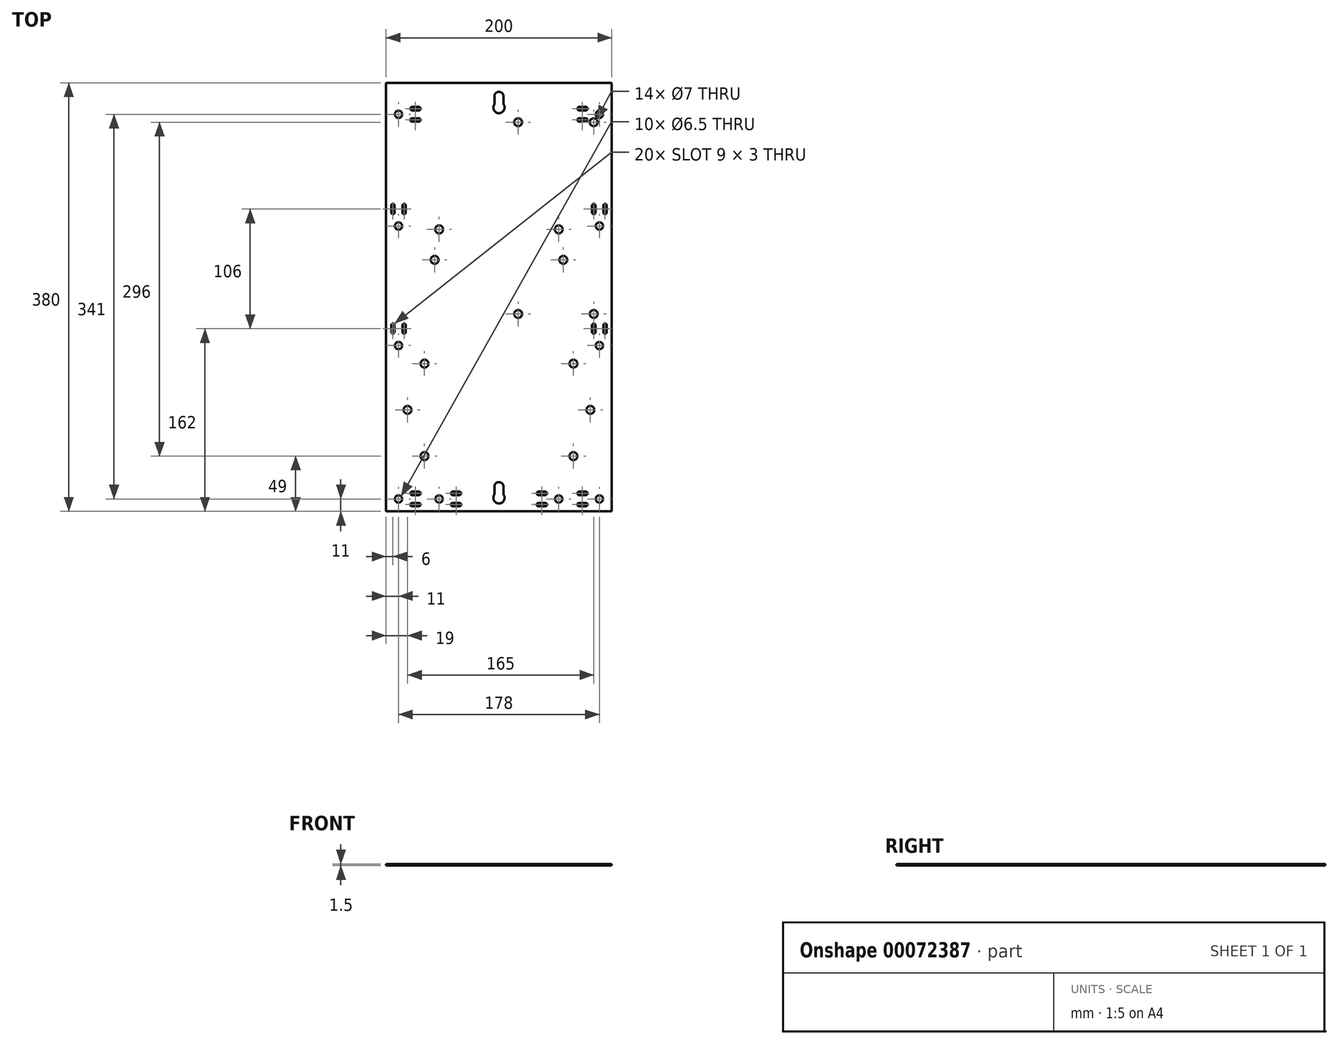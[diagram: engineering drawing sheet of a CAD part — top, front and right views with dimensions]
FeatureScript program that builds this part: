
annotation { "Feature Type Name" : "Feature", "Feature Type Description" : "" }
export const myFeature = defineFeature(function(context is Context, id is Id, definition is map)
    precondition{}
    {
        {
            var Q0;
            Q0=qCreatedBy(makeId("Top.planeOp"),FACE);
            var sketch = newSketch(context, id + "F0", { "sketchPlane" : qUnion([Q0])});
            skLineSegment(sketch, "E0.rect.bottom", {"start": v(100, 190) * mm, "end": v(-100, 190) * mm});
            skLineSegment(sketch, "E0.rect.top", {"start": v(100, -190) * mm, "end": v(-100, -190) * mm});
            skLineSegment(sketch, "E0.rect.left", {"start": v(100, 190) * mm, "end": v(100, -190) * mm});
            skLineSegment(sketch, "E0.rect.right", {"start": v(-100, 190) * mm, "end": v(-100, -190) * mm});
            skPoint(sketch, "E0.rect.middle", {"position": v(0, 0) * mm});
            skLineSegment(sketch, "E1", {"start": v(0, -190) * mm, "end": v(0, 190) * mm, "construction": true});
            skCircle(sketch, "E2", {"center": v(-89, 162) * mm, "radius": 3.25 * mm});
            skCircle(sketch, "E3", {"center": v(-89, 63) * mm, "radius": 3.25 * mm});
            skCircle(sketch, "E4", {"center": v(-89, -43) * mm, "radius": 3.25 * mm});
            skCircle(sketch, "E5", {"center": v(-89, -179) * mm, "radius": 3.25 * mm});
            skCircle(sketch, "E6", {"center": v(-66, -141) * mm, "radius": 3.5 * mm});
            skCircle(sketch, "E7", {"center": v(-81, -100) * mm, "radius": 3.5 * mm});
            skCircle(sketch, "E8", {"center": v(-66, -59) * mm, "radius": 3.5 * mm});
            skCircle(sketch, "E9", {"center": v(-57, 33) * mm, "radius": 3.5 * mm});
            skCircle(sketch, "E10", {"center": v(-53, 60) * mm, "radius": 3.5 * mm});
            skCircle(sketch, "E11", {"center": v(-53, -179) * mm, "radius": 3.25 * mm});
            skArc(sketch, "E12", {"start": v(-77, -172.5) * mm, "mid": v(-78.5, -174) * mm, "end": v(-77, -175.5) * mm});
            skArc(sketch, "E13", {"start": v(-71, -175.5) * mm, "mid": v(-69.5, -174) * mm, "end": v(-71, -172.5) * mm});
            skLineSegment(sketch, "E14", {"start": v(-77, -172.5) * mm, "end": v(-71, -172.5) * mm});
            skLineSegment(sketch, "E15", {"start": v(-71, -175.5) * mm, "end": v(-77, -175.5) * mm});
            skLineSegment(sketch, "E16", {"start": v(-89, -179) * mm, "end": v(-66.78, -179) * mm, "construction": true});
            skArc(sketch, "E17.MirrorCS", {"start": v(-71, -182.5) * mm, "mid": v(-69.5, -184) * mm, "end": v(-71, -185.5) * mm});
            skLineSegment(sketch, "E18.MirrorCS", {"start": v(-77, -185.5) * mm, "end": v(-71, -185.5) * mm});
            skLineSegment(sketch, "E19.MirrorCS", {"start": v(-71, -182.5) * mm, "end": v(-77, -182.5) * mm});
            skArc(sketch, "E20.MirrorCS", {"start": v(-77, -185.5) * mm, "mid": v(-78.5, -184) * mm, "end": v(-77, -182.5) * mm});
            skArc(sketch, "E21.1.0.0", {"start": v(-41, -172.5) * mm, "mid": v(-42.5, -174) * mm, "end": v(-41, -175.5) * mm});
            skLineSegment(sketch, "E21.1.0.1", {"start": v(-41, -172.5) * mm, "end": v(-35, -172.5) * mm});
            skLineSegment(sketch, "E21.1.0.2", {"start": v(-35, -182.5) * mm, "end": v(-41, -182.5) * mm});
            skArc(sketch, "E21.1.0.3", {"start": v(-41, -185.5) * mm, "mid": v(-42.5, -184) * mm, "end": v(-41, -182.5) * mm});
            skLineSegment(sketch, "E21.1.0.4", {"start": v(-41, -185.5) * mm, "end": v(-35, -185.5) * mm});
            skArc(sketch, "E21.1.0.5", {"start": v(-35, -182.5) * mm, "mid": v(-33.5, -184) * mm, "end": v(-35, -185.5) * mm});
            skLineSegment(sketch, "E21.1.0.6", {"start": v(-35, -175.5) * mm, "end": v(-41, -175.5) * mm});
            skArc(sketch, "E21.1.0.7", {"start": v(-35, -175.5) * mm, "mid": v(-33.5, -174) * mm, "end": v(-35, -172.5) * mm});
            skLineSegment(sketch, "E21.direction1", {"start": v(-77, -175.5) * mm, "end": v(-41, -175.5) * mm, "construction": true});
            skArc(sketch, "E22", {"start": v(-95.5, -31) * mm, "mid": v(-94, -32.5) * mm, "end": v(-92.5, -31) * mm});
            skArc(sketch, "E23", {"start": v(-92.5, -25) * mm, "mid": v(-94, -23.5) * mm, "end": v(-95.5, -25) * mm});
            skLineSegment(sketch, "E24", {"start": v(-95.5, -31) * mm, "end": v(-95.5, -25) * mm});
            skLineSegment(sketch, "E25", {"start": v(-92.5, -25) * mm, "end": v(-92.5, -31) * mm});
            skLineSegment(sketch, "E26", {"start": v(-89, -43) * mm, "end": v(-89, -23.5) * mm, "construction": true});
            skArc(sketch, "E27.MirrorCS", {"start": v(-85.5, -25) * mm, "mid": v(-84, -23.5) * mm, "end": v(-82.5, -25) * mm});
            skLineSegment(sketch, "E28.MirrorCS", {"start": v(-85.5, -25) * mm, "end": v(-85.5, -31) * mm});
            skLineSegment(sketch, "E29.MirrorCS", {"start": v(-82.5, -31) * mm, "end": v(-82.5, -25) * mm});
            skArc(sketch, "E30.MirrorCS", {"start": v(-82.5, -31) * mm, "mid": v(-84, -32.5) * mm, "end": v(-85.5, -31) * mm});
            skLineSegment(sketch, "E31.0.1.0", {"start": v(-85.5, 81) * mm, "end": v(-85.5, 75) * mm});
            skLineSegment(sketch, "E31.0.1.1", {"start": v(-92.5, 81) * mm, "end": v(-92.5, 75) * mm});
            skLineSegment(sketch, "E31.0.1.2", {"start": v(-95.5, 75) * mm, "end": v(-95.5, 81) * mm});
            skArc(sketch, "E31.0.1.3", {"start": v(-95.5, 75) * mm, "mid": v(-94, 73.5) * mm, "end": v(-92.5, 75) * mm});
            skLineSegment(sketch, "E31.0.1.4", {"start": v(-82.5, 75) * mm, "end": v(-82.5, 81) * mm});
            skArc(sketch, "E31.0.1.5", {"start": v(-82.5, 75) * mm, "mid": v(-84, 73.5) * mm, "end": v(-85.5, 75) * mm});
            skArc(sketch, "E31.0.1.6", {"start": v(-85.5, 81) * mm, "mid": v(-84, 82.5) * mm, "end": v(-82.5, 81) * mm});
            skArc(sketch, "E31.0.1.7", {"start": v(-92.5, 81) * mm, "mid": v(-94, 82.5) * mm, "end": v(-95.5, 81) * mm});
            skLineSegment(sketch, "E31.direction1", {"start": v(-85.5, -31) * mm, "end": v(-60.5, -31) * mm, "construction": true});
            skLineSegment(sketch, "E31.direction2", {"start": v(-85.5, -31) * mm, "end": v(-85.5, 75) * mm, "construction": true});
            skArc(sketch, "E32", {"start": v(-77, 168.5) * mm, "mid": v(-78.5, 167) * mm, "end": v(-77, 165.5) * mm});
            skArc(sketch, "E33", {"start": v(-71, 165.5) * mm, "mid": v(-69.5, 167) * mm, "end": v(-71, 168.5) * mm});
            skLineSegment(sketch, "E34", {"start": v(-77, 168.5) * mm, "end": v(-71, 168.5) * mm});
            skLineSegment(sketch, "E35", {"start": v(-71, 165.5) * mm, "end": v(-77, 165.5) * mm});
            skLineSegment(sketch, "E36", {"start": v(-89, 162) * mm, "end": v(-66.49, 162) * mm, "construction": true});
            skLineSegment(sketch, "E37.MirrorCS", {"start": v(-71, 158.5) * mm, "end": v(-77, 158.5) * mm});
            skLineSegment(sketch, "E38.MirrorCS", {"start": v(-77, 155.5) * mm, "end": v(-71, 155.5) * mm});
            skArc(sketch, "E39.MirrorCS", {"start": v(-71, 158.5) * mm, "mid": v(-69.5, 157) * mm, "end": v(-71, 155.5) * mm});
            skArc(sketch, "E40.MirrorCS", {"start": v(-77, 155.5) * mm, "mid": v(-78.5, 157) * mm, "end": v(-77, 158.5) * mm});
            skArc(sketch, "E41.MirrorCS", {"start": v(92.5, -25) * mm, "mid": v(94, -23.5) * mm, "end": v(95.5, -25) * mm});
            skArc(sketch, "E42.MirrorCS", {"start": v(95.5, -31) * mm, "mid": v(94, -32.5) * mm, "end": v(92.5, -31) * mm});
            skLineSegment(sketch, "E43.MirrorCS", {"start": v(95.5, -31) * mm, "end": v(95.5, -25) * mm});
            skLineSegment(sketch, "E44.MirrorCS", {"start": v(92.5, -25) * mm, "end": v(92.5, -31) * mm});
            skLineSegment(sketch, "E45.MirrorCS", {"start": v(71, -175.5) * mm, "end": v(77, -175.5) * mm});
            skLineSegment(sketch, "E46.MirrorCS", {"start": v(41, -172.5) * mm, "end": v(35, -172.5) * mm});
            skArc(sketch, "E47.MirrorCS", {"start": v(82.5, -31) * mm, "mid": v(84, -32.5) * mm, "end": v(85.5, -31) * mm});
            skArc(sketch, "E48.MirrorCS", {"start": v(92.5, 81) * mm, "mid": v(94, 82.5) * mm, "end": v(95.5, 81) * mm});
            skLineSegment(sketch, "E49.MirrorCS", {"start": v(77, -172.5) * mm, "end": v(71, -172.5) * mm});
            skArc(sketch, "E50.MirrorCS", {"start": v(41, -172.5) * mm, "mid": v(42.5, -174) * mm, "end": v(41, -175.5) * mm});
            skLineSegment(sketch, "E51.MirrorCS", {"start": v(82.5, -31) * mm, "end": v(82.5, -25) * mm});
            skArc(sketch, "E52.MirrorCS", {"start": v(77, -172.5) * mm, "mid": v(78.5, -174) * mm, "end": v(77, -175.5) * mm});
            skArc(sketch, "E53.MirrorCS", {"start": v(85.5, -25) * mm, "mid": v(84, -23.5) * mm, "end": v(82.5, -25) * mm});
            skLineSegment(sketch, "E54.MirrorCS", {"start": v(77, 168.5) * mm, "end": v(71, 168.5) * mm});
            skLineSegment(sketch, "E55.MirrorCS", {"start": v(71, -182.5) * mm, "end": v(77, -182.5) * mm});
            skLineSegment(sketch, "E56.MirrorCS", {"start": v(35, -182.5) * mm, "end": v(41, -182.5) * mm});
            skLineSegment(sketch, "E57.MirrorCS", {"start": v(85.5, 81) * mm, "end": v(85.5, 75) * mm});
            skLineSegment(sketch, "E58.MirrorCS", {"start": v(95.5, 75) * mm, "end": v(95.5, 81) * mm});
            skLineSegment(sketch, "E59.MirrorCS", {"start": v(77, -185.5) * mm, "end": v(71, -185.5) * mm});
            skArc(sketch, "E60.MirrorCS", {"start": v(95.5, 75) * mm, "mid": v(94, 73.5) * mm, "end": v(92.5, 75) * mm});
            skLineSegment(sketch, "E61.MirrorCS", {"start": v(85.5, -25) * mm, "end": v(85.5, -31) * mm});
            skArc(sketch, "E62.MirrorCS", {"start": v(77, 168.5) * mm, "mid": v(78.5, 167) * mm, "end": v(77, 165.5) * mm});
            skLineSegment(sketch, "E63.MirrorCS", {"start": v(92.5, 81) * mm, "end": v(92.5, 75) * mm});
            skArc(sketch, "E64.MirrorCS", {"start": v(71, -182.5) * mm, "mid": v(69.5, -184) * mm, "end": v(71, -185.5) * mm});
            skArc(sketch, "E65.MirrorCS", {"start": v(71, 165.5) * mm, "mid": v(69.5, 167) * mm, "end": v(71, 168.5) * mm});
            skLineSegment(sketch, "E66.MirrorCS", {"start": v(71, 165.5) * mm, "end": v(77, 165.5) * mm});
            skLineSegment(sketch, "E67.MirrorCS", {"start": v(35, -175.5) * mm, "end": v(41, -175.5) * mm});
            skLineSegment(sketch, "E68.MirrorCS", {"start": v(71, 158.5) * mm, "end": v(77, 158.5) * mm});
            skArc(sketch, "E69.MirrorCS", {"start": v(35, -175.5) * mm, "mid": v(33.5, -174) * mm, "end": v(35, -172.5) * mm});
            skArc(sketch, "E70.MirrorCS", {"start": v(82.5, 75) * mm, "mid": v(84, 73.5) * mm, "end": v(85.5, 75) * mm});
            skArc(sketch, "E71.MirrorCS", {"start": v(85.5, 81) * mm, "mid": v(84, 82.5) * mm, "end": v(82.5, 81) * mm});
            skLineSegment(sketch, "E72.MirrorCS", {"start": v(77, 155.5) * mm, "end": v(71, 155.5) * mm});
            skArc(sketch, "E73.MirrorCS", {"start": v(77, 155.5) * mm, "mid": v(78.5, 157) * mm, "end": v(77, 158.5) * mm});
            skLineSegment(sketch, "E74.MirrorCS", {"start": v(41, -185.5) * mm, "end": v(35, -185.5) * mm});
            skArc(sketch, "E75.MirrorCS", {"start": v(71, -175.5) * mm, "mid": v(69.5, -174) * mm, "end": v(71, -172.5) * mm});
            skArc(sketch, "E76.MirrorCS", {"start": v(35, -182.5) * mm, "mid": v(33.5, -184) * mm, "end": v(35, -185.5) * mm});
            skArc(sketch, "E77.MirrorCS", {"start": v(41, -185.5) * mm, "mid": v(42.5, -184) * mm, "end": v(41, -182.5) * mm});
            skArc(sketch, "E78.MirrorCS", {"start": v(77, -185.5) * mm, "mid": v(78.5, -184) * mm, "end": v(77, -182.5) * mm});
            skLineSegment(sketch, "E79.MirrorCS", {"start": v(82.5, 75) * mm, "end": v(82.5, 81) * mm});
            skArc(sketch, "E80.MirrorCS", {"start": v(71, 158.5) * mm, "mid": v(69.5, 157) * mm, "end": v(71, 155.5) * mm});
            skLineSegment(sketch, "E81.MirrorCS", {"start": v(89, -43) * mm, "end": v(89, -23.5) * mm, "construction": true});
            skLineSegment(sketch, "E82.MirrorCS", {"start": v(89, 162) * mm, "end": v(66.49, 162) * mm, "construction": true});
            skCircle(sketch, "E83.MirrorC", {"center": v(53, -179) * mm, "radius": 3.25 * mm});
            skLineSegment(sketch, "E84.MirrorCS", {"start": v(77, -175.5) * mm, "end": v(41, -175.5) * mm, "construction": true});
            skLineSegment(sketch, "E85.MirrorCS", {"start": v(89, -179) * mm, "end": v(66.78, -179) * mm, "construction": true});
            skCircle(sketch, "E86.MirrorC", {"center": v(89, -43) * mm, "radius": 3.25 * mm});
            skCircle(sketch, "E87.MirrorC", {"center": v(89, -179) * mm, "radius": 3.25 * mm});
            skCircle(sketch, "E88.MirrorC", {"center": v(89, 162) * mm, "radius": 3.25 * mm});
            skLineSegment(sketch, "E89.MirrorCS", {"start": v(85.5, -31) * mm, "end": v(85.5, 75) * mm, "construction": true});
            skLineSegment(sketch, "E90.MirrorCS", {"start": v(85.5, -31) * mm, "end": v(60.5, -31) * mm, "construction": true});
            skCircle(sketch, "E91.MirrorC", {"center": v(53, 60) * mm, "radius": 3.5 * mm});
            skCircle(sketch, "E92.MirrorC", {"center": v(89, 63) * mm, "radius": 3.25 * mm});
            skCircle(sketch, "E93.MirrorC", {"center": v(66, -141) * mm, "radius": 3.5 * mm});
            skCircle(sketch, "E94.MirrorC", {"center": v(81, -100) * mm, "radius": 3.5 * mm});
            skCircle(sketch, "E95.MirrorC", {"center": v(57, 33) * mm, "radius": 3.5 * mm});
            skCircle(sketch, "E96.MirrorC", {"center": v(66, -59) * mm, "radius": 3.5 * mm});
            skSolve(sketch);
        }
        {
            var Q0;
            Q0=makeQuery(id+"F0.imprint","IMPRINT",FACE,{"disambiguationData":[TD([[makeQuery(id+"F0.imprint","IMPRINT",EDGE,{"derivedFrom":sQuery(id+"F0.wireOp",EDGE,"E0.rect.bottom")}),1.0]])]});
            extrude(context, id + "F1", {"entities" : qUnion([Q0]), "depth" : 1.5 * mm});
        }
        {
            var Q0;
            Q0=makeQuery(id+"F1.opExtrude","CAP_FACE",FACE,{"disambiguationData":[OSD([sQuery(id+"F0.wireOp",EDGE,"E0.rect.bottom"),sQuery(id+"F0.wireOp",EDGE,"E0.rect.top"),sQuery(id+"F0.wireOp",EDGE,"E0.rect.left"),sQuery(id+"F0.wireOp",EDGE,"E0.rect.right"),sQuery(id+"F0.wireOp",EDGE,"E2"),sQuery(id+"F0.wireOp",EDGE,"E3"),sQuery(id+"F0.wireOp",EDGE,"E4"),sQuery(id+"F0.wireOp",EDGE,"E5"),sQuery(id+"F0.wireOp",EDGE,"E6"),sQuery(id+"F0.wireOp",EDGE,"E7"),sQuery(id+"F0.wireOp",EDGE,"E8"),sQuery(id+"F0.wireOp",EDGE,"E9"),sQuery(id+"F0.wireOp",EDGE,"E10"),sQuery(id+"F0.wireOp",EDGE,"E11"),sQuery(id+"F0.wireOp",EDGE,"E12"),sQuery(id+"F0.wireOp",EDGE,"E13"),sQuery(id+"F0.wireOp",EDGE,"E14"),sQuery(id+"F0.wireOp",EDGE,"E15"),sQuery(id+"F0.wireOp",EDGE,"E17.MirrorCS"),sQuery(id+"F0.wireOp",EDGE,"E18.MirrorCS"),sQuery(id+"F0.wireOp",EDGE,"E19.MirrorCS"),sQuery(id+"F0.wireOp",EDGE,"E20.MirrorCS"),sQuery(id+"F0.wireOp",EDGE,"E21.1.0.0"),sQuery(id+"F0.wireOp",EDGE,"E21.1.0.1"),sQuery(id+"F0.wireOp",EDGE,"E21.1.0.2"),sQuery(id+"F0.wireOp",EDGE,"E21.1.0.3"),sQuery(id+"F0.wireOp",EDGE,"E21.1.0.4"),sQuery(id+"F0.wireOp",EDGE,"E21.1.0.5"),sQuery(id+"F0.wireOp",EDGE,"E21.1.0.6"),sQuery(id+"F0.wireOp",EDGE,"E21.1.0.7"),sQuery(id+"F0.wireOp",EDGE,"E22"),sQuery(id+"F0.wireOp",EDGE,"E23"),sQuery(id+"F0.wireOp",EDGE,"E24"),sQuery(id+"F0.wireOp",EDGE,"E25"),sQuery(id+"F0.wireOp",EDGE,"E27.MirrorCS"),sQuery(id+"F0.wireOp",EDGE,"E28.MirrorCS"),sQuery(id+"F0.wireOp",EDGE,"E29.MirrorCS"),sQuery(id+"F0.wireOp",EDGE,"E30.MirrorCS"),sQuery(id+"F0.wireOp",EDGE,"E31.0.1.0"),sQuery(id+"F0.wireOp",EDGE,"E31.0.1.1"),sQuery(id+"F0.wireOp",EDGE,"E31.0.1.2"),sQuery(id+"F0.wireOp",EDGE,"E31.0.1.3"),sQuery(id+"F0.wireOp",EDGE,"E31.0.1.4"),sQuery(id+"F0.wireOp",EDGE,"E31.0.1.5"),sQuery(id+"F0.wireOp",EDGE,"E31.0.1.6"),sQuery(id+"F0.wireOp",EDGE,"E31.0.1.7"),sQuery(id+"F0.wireOp",EDGE,"E32"),sQuery(id+"F0.wireOp",EDGE,"E33"),sQuery(id+"F0.wireOp",EDGE,"E34"),sQuery(id+"F0.wireOp",EDGE,"E35"),sQuery(id+"F0.wireOp",EDGE,"E37.MirrorCS"),sQuery(id+"F0.wireOp",EDGE,"E38.MirrorCS"),sQuery(id+"F0.wireOp",EDGE,"E39.MirrorCS"),sQuery(id+"F0.wireOp",EDGE,"E40.MirrorCS"),sQuery(id+"F0.wireOp",EDGE,"E41.MirrorCS"),sQuery(id+"F0.wireOp",EDGE,"E42.MirrorCS"),sQuery(id+"F0.wireOp",EDGE,"E43.MirrorCS"),sQuery(id+"F0.wireOp",EDGE,"E44.MirrorCS"),sQuery(id+"F0.wireOp",EDGE,"E45.MirrorCS"),sQuery(id+"F0.wireOp",EDGE,"E46.MirrorCS"),sQuery(id+"F0.wireOp",EDGE,"E47.MirrorCS"),sQuery(id+"F0.wireOp",EDGE,"E48.MirrorCS"),sQuery(id+"F0.wireOp",EDGE,"E49.MirrorCS"),sQuery(id+"F0.wireOp",EDGE,"E50.MirrorCS"),sQuery(id+"F0.wireOp",EDGE,"E51.MirrorCS"),sQuery(id+"F0.wireOp",EDGE,"E52.MirrorCS"),sQuery(id+"F0.wireOp",EDGE,"E53.MirrorCS"),sQuery(id+"F0.wireOp",EDGE,"E54.MirrorCS"),sQuery(id+"F0.wireOp",EDGE,"E55.MirrorCS"),sQuery(id+"F0.wireOp",EDGE,"E56.MirrorCS"),sQuery(id+"F0.wireOp",EDGE,"E57.MirrorCS"),sQuery(id+"F0.wireOp",EDGE,"E58.MirrorCS"),sQuery(id+"F0.wireOp",EDGE,"E59.MirrorCS"),sQuery(id+"F0.wireOp",EDGE,"E60.MirrorCS"),sQuery(id+"F0.wireOp",EDGE,"E61.MirrorCS"),sQuery(id+"F0.wireOp",EDGE,"E62.MirrorCS"),sQuery(id+"F0.wireOp",EDGE,"E63.MirrorCS"),sQuery(id+"F0.wireOp",EDGE,"E64.MirrorCS"),sQuery(id+"F0.wireOp",EDGE,"E65.MirrorCS"),sQuery(id+"F0.wireOp",EDGE,"E66.MirrorCS"),sQuery(id+"F0.wireOp",EDGE,"E67.MirrorCS"),sQuery(id+"F0.wireOp",EDGE,"E68.MirrorCS"),sQuery(id+"F0.wireOp",EDGE,"E69.MirrorCS"),sQuery(id+"F0.wireOp",EDGE,"E70.MirrorCS"),sQuery(id+"F0.wireOp",EDGE,"E71.MirrorCS"),sQuery(id+"F0.wireOp",EDGE,"E72.MirrorCS"),sQuery(id+"F0.wireOp",EDGE,"E73.MirrorCS"),sQuery(id+"F0.wireOp",EDGE,"E74.MirrorCS"),sQuery(id+"F0.wireOp",EDGE,"E75.MirrorCS"),sQuery(id+"F0.wireOp",EDGE,"E76.MirrorCS"),sQuery(id+"F0.wireOp",EDGE,"E77.MirrorCS"),sQuery(id+"F0.wireOp",EDGE,"E78.MirrorCS"),sQuery(id+"F0.wireOp",EDGE,"E79.MirrorCS"),sQuery(id+"F0.wireOp",EDGE,"E80.MirrorCS"),sQuery(id+"F0.wireOp",EDGE,"E83.MirrorC"),sQuery(id+"F0.wireOp",EDGE,"E86.MirrorC"),sQuery(id+"F0.wireOp",EDGE,"E87.MirrorC"),sQuery(id+"F0.wireOp",EDGE,"E88.MirrorC"),sQuery(id+"F0.wireOp",EDGE,"E91.MirrorC"),sQuery(id+"F0.wireOp",EDGE,"E92.MirrorC"),sQuery(id+"F0.wireOp",EDGE,"E93.MirrorC"),sQuery(id+"F0.wireOp",EDGE,"E94.MirrorC"),sQuery(id+"F0.wireOp",EDGE,"E95.MirrorC"),sQuery(id+"F0.wireOp",EDGE,"E96.MirrorC")])],"isStart":false});
            var sketch = newSketch(context, id + "F2", { "sketchPlane" : qUnion([Q0])});
            skCircle(sketch, "E97", {"center": v(84, -15) * mm, "radius": 3.5 * mm});
            skCircle(sketch, "E98", {"center": v(17, -15) * mm, "radius": 3.5 * mm});
            skArc(sketch, "E99", {"start": v(4, 178) * mm, "mid": v(0, 182) * mm, "end": v(-4, 178) * mm});
            skPoint(sketch, "E99.centerSnap0", {"position": v(0, 190) * mm});
            skArc(sketch, "E100", {"start": v(-4, 171) * mm, "mid": v(0, 163) * mm, "end": v(4, 171) * mm});
            skLineSegment(sketch, "E101", {"start": v(4, 178) * mm, "end": v(4, 171) * mm});
            skLineSegment(sketch, "E102", {"start": v(-4, 178) * mm, "end": v(-4, 171) * mm});
            skArc(sketch, "E103", {"start": v(-4, -175) * mm, "mid": v(0, -183) * mm, "end": v(4, -175) * mm});
            skPoint(sketch, "E103.centerSnap0", {"position": v(0, -190) * mm});
            skArc(sketch, "E104", {"start": v(4, -168) * mm, "mid": v(0, -164) * mm, "end": v(-4, -168) * mm});
            skLineSegment(sketch, "E105", {"start": v(4, -168) * mm, "end": v(4, -175) * mm});
            skLineSegment(sketch, "E106", {"start": v(-4, -168) * mm, "end": v(-4, -175) * mm});
            skCircle(sketch, "E107", {"center": v(84, 155) * mm, "radius": 3.5 * mm});
            skCircle(sketch, "E108", {"center": v(17, 155) * mm, "radius": 3.5 * mm});
            skSolve(sketch);
        }
        {
            var Q0;
            Q0 = qSketchRegion(id + "F2", true);
            extrude(context, id + "F3", {"entities" : qUnion([Q0]), "operationType" : NewBodyOperationType.REMOVE, "oppositeDirection" : true, "depth" : 25 * mm});
        }
    });
